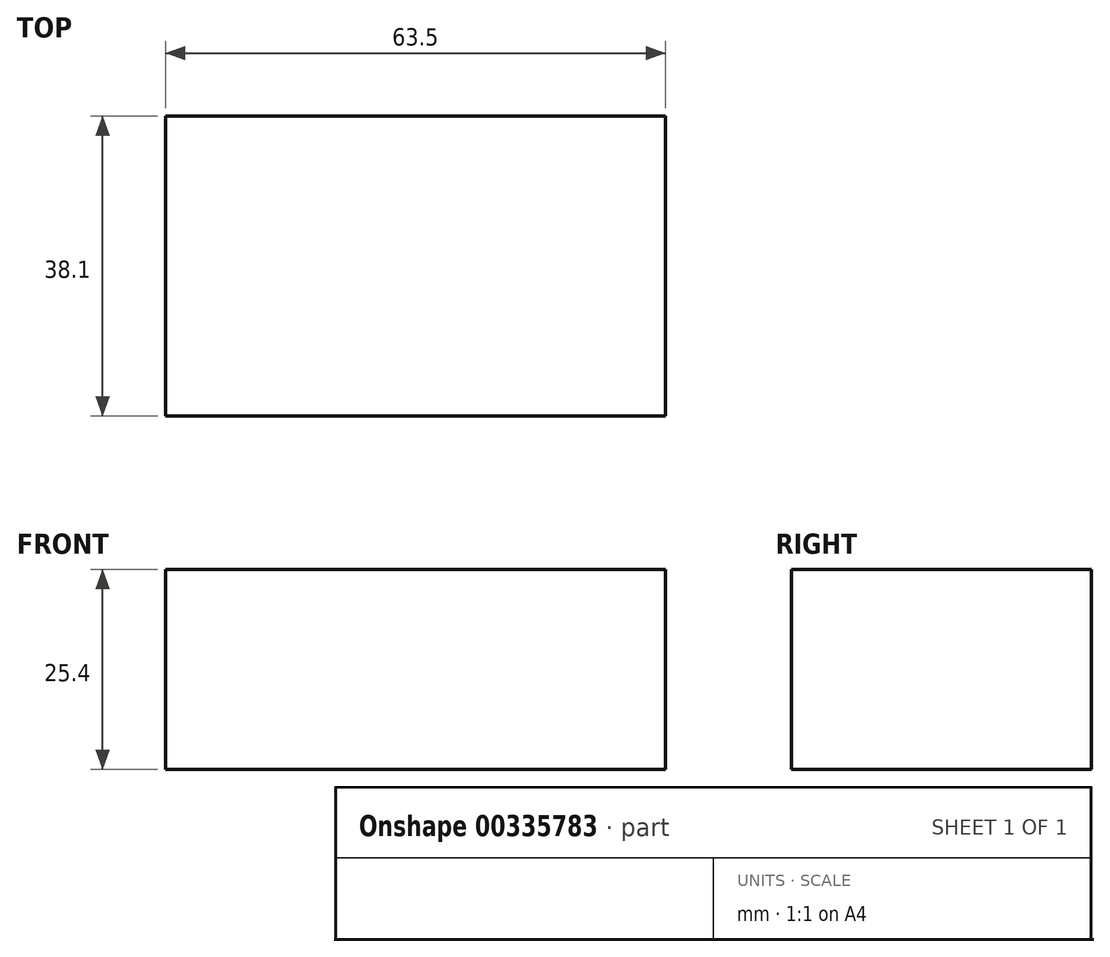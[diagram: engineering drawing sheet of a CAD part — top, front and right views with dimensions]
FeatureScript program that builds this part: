
annotation { "Feature Type Name" : "Feature", "Feature Type Description" : "" }
export const myFeature = defineFeature(function(context is Context, id is Id, definition is map)
    precondition{}
    {
        {
            var Q0;
            Q0=qCreatedBy(makeId("Top.planeOp"),FACE);
            var sketch = newSketch(context, id + "F0", { "sketchPlane" : qUnion([Q0])});
            skLineSegment(sketch, "E0", {"start": v(0, 0) * mm, "end": v(-63.5, 0) * mm});
            skLineSegment(sketch, "E1", {"start": v(-63.5, 0) * mm, "end": v(-63.5, 38.1) * mm});
            skLineSegment(sketch, "E2", {"start": v(-63.5, 38.1) * mm, "end": v(0, 38.1) * mm});
            skLineSegment(sketch, "E3", {"start": v(0, 38.1) * mm, "end": v(0, 0) * mm});
            skSolve(sketch);
        }
        {
            var Q0;
            Q0=makeQuery(id+"F0.imprint","IMPRINT",FACE,{"disambiguationData":[TD([[makeQuery(id+"F0.imprint","IMPRINT",EDGE,{"derivedFrom":sQuery(id+"F0.wireOp",EDGE,"E0")}),-1.0]])]});
            extrude(context, id + "F1", {"entities" : qUnion([Q0]), "depth" : 25.4 * mm});
        }
        {
            var Q0;
            Q0=makeQuery(id+"F1.opExtrude","CAP_FACE",FACE,{"disambiguationData":[OSD([sQuery(id+"F0.wireOp",EDGE,"E0"),sQuery(id+"F0.wireOp",EDGE,"E1"),sQuery(id+"F0.wireOp",EDGE,"E2"),sQuery(id+"F0.wireOp",EDGE,"E3")])],"isStart":true});
            var sketch = newSketch(context, id + "F2", { "sketchPlane" : qUnion([Q0])});
            skLineSegment(sketch, "E4.bottom", {"start": v(-63.5, 0) * mm, "end": v(-74.48, 0) * mm});
            skLineSegment(sketch, "E4.top", {"start": v(-63.5, -38.1) * mm, "end": v(-74.48, -38.1) * mm});
            skLineSegment(sketch, "E4.left", {"start": v(-63.5, 0) * mm, "end": v(-63.5, -38.1) * mm});
            skLineSegment(sketch, "E4.right", {"start": v(-74.48, 0) * mm, "end": v(-74.48, -38.1) * mm});
            skSolve(sketch);
        }
        {
            var Q0;
            Q0=sQuery(id+"F2.wireOp",EDGE,"E4.right");
            var Q1;
            Q1=sQuery(id+"F2.wireOp",EDGE,"E4.bottom");
            var Q2;
            Q2=sQuery(id+"F2.wireOp",EDGE,"E4.left");
            var Q3;
            Q3=sQuery(id+"F2.wireOp",EDGE,"E4.top");
            extrude(context, id + "F3", {"bodyType" : ToolBodyType.SURFACE, "surfaceEntities" : qUnion([Q0, Q1, Q2, Q3]), "oppositeDirection" : true, "depth" : 1.14 * mm});
        }
    });
